# Revit family: Chair-Multi_Purpose-Allermuir-Phoulds PH1
name_source: partatom
category: Furniture
revit_build: Autodesk Revit Architecture 2012 (Build: 20110309_2315(x64)
units: mm (PartAtom-declared; Revit-internal decimal feet)

## types (1)
- PH1
    04 CSI = 12 51 00
    2.5" Casters = No
    95 CSI = 12510
    Advanced Sync Tilt with Multi Position Back = No
    Airflow Back Mesh = No
    Arm Height = 25 1/8"
    Assembly Code = E2020200
    Base = Metal - Allermuir - Chrome - Polished
    Black Components = Yes
    Black GRP Base = No
    Black Gas Lift = No
    Black Plastic Back Membrane = No
    Color Availability = See price list for material options
    Cushion = Plastic - Allermuir - Canvas - Brown
    Detachable writing table = No
    Fabric Spec Sheets = http://www.allermuir.net
    Glides = Fabric - Allermuir - Smooth -Pebbled - Black
    Height Adjustable Arms = No
    Height Adjustable Arms with Multi funtction Pad = No
    Leg = Metal - Allermuir - Chrome - Polished
    Manufacturer = Allermuir
    Manufacturer Fax = (419) 887 5805
    Model = PH1
    Negative Seat Tilt = No
    Optional Feature Notes = Retracktable linking facility, soft touchh arm pads, polished aluminum frame
    Overall Depth = 22 1/4"
    Overall Height = 35"
    Overall Width = 23 1/2"
    Plugin Data URL = http://products.ecoscorecard.com
    Product Line = Phoulds
    Product Page URL = http://www.allermuir.net
    Seat = Fabric - Allermuir - Smooth -Pebbled - Black
    Seat Depth = 18 1/2"
    Seat Depth Adjustment = No
    Seat Height = 16 1/8"
    Seat Width = 19 1/4"
    Seat or Base = Fabric - Allermuir - Smooth -Pebbled - Black
    Stacks = No
    Subcategory = Multi-Purpose
    URL = http://www.allermuir.net
    Weight = 18.0 lb
    ecoScorecard Product Page = http://products.ecoscorecard.com
    ecoScorecard_data = http://thesenatorgroup.ecoscorecard.com

## geometry (parser evidence)
native form markers: Blend x14, Sweep x2
no freeform markers — native parametric forms only
